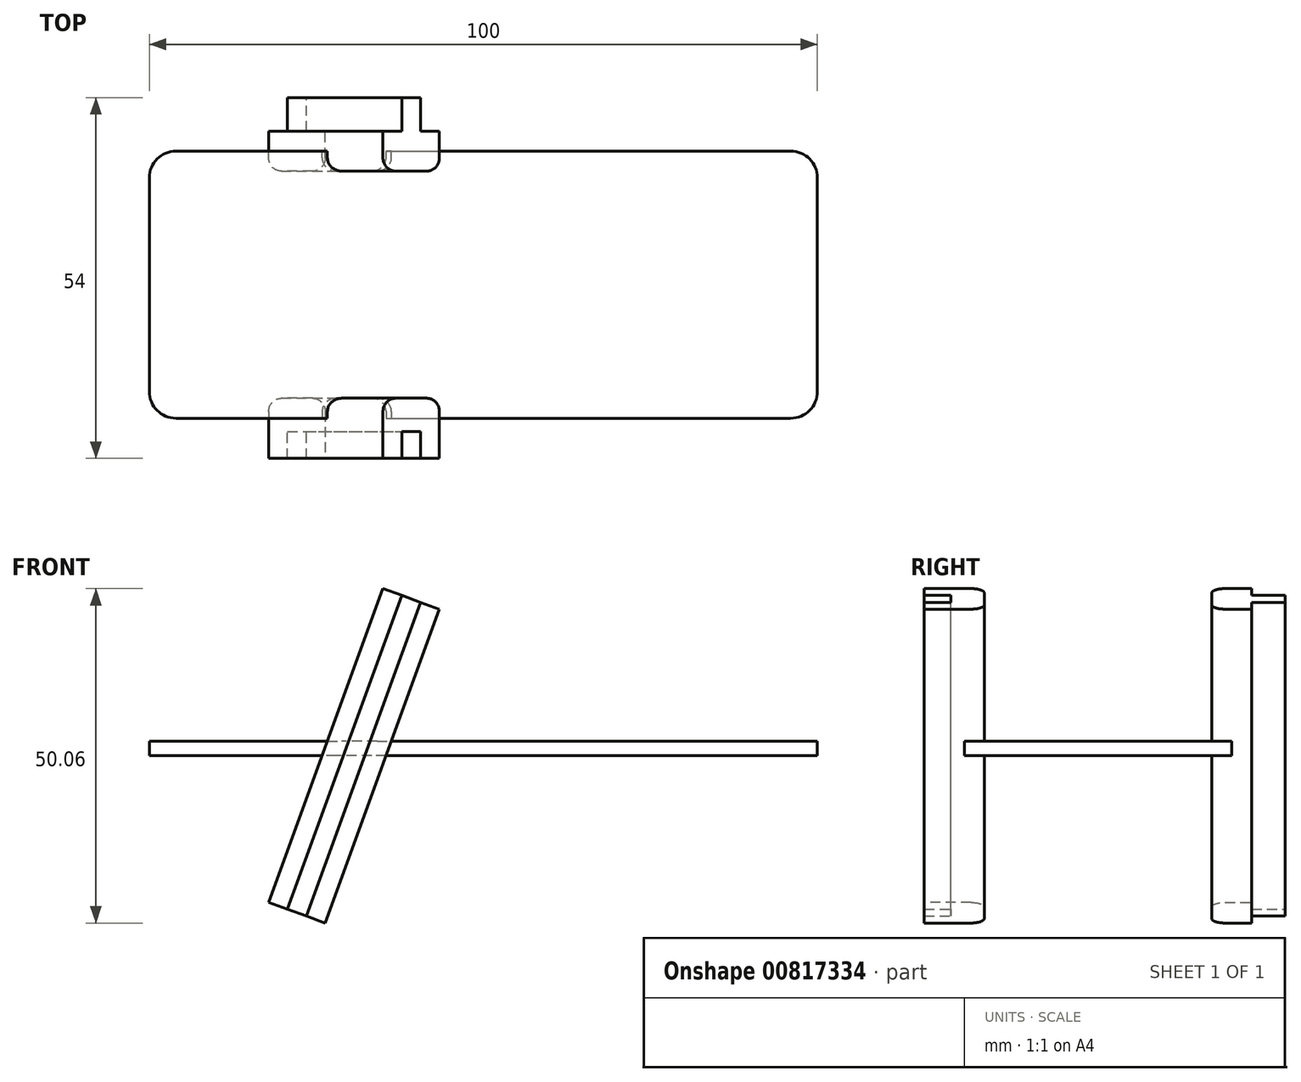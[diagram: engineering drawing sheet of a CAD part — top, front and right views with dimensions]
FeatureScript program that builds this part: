
annotation { "Feature Type Name" : "Feature", "Feature Type Description" : "" }
export const myFeature = defineFeature(function(context is Context, id is Id, definition is map)
    precondition{}
    {
        {
            var Q0;
            Q0=qCreatedBy(makeId("Top.planeOp"),FACE);
            var sketch = newSketch(context, id + "F0", { "sketchPlane" : qUnion([Q0])});
            skLineSegment(sketch, "E0.bottom", {"start": v(-43.22, 17.39) * mm, "end": v(-12.57, 17.39) * mm});
            skLineSegment(sketch, "E0.top", {"start": v(-43.22, -22.61) * mm, "end": v(-12.57, -22.61) * mm});
            skLineSegment(sketch, "E0.left", {"start": v(-43.22, 17.39) * mm, "end": v(-43.22, -22.61) * mm});
            skLineSegment(sketch, "E1", {"start": v(-12.57, 17.39) * mm, "end": v(-12.57, -22.61) * mm});
            skLineSegment(sketch, "E2", {"start": v(-12.57, 17.39) * mm, "end": v(56.78, 17.39) * mm});
            skLineSegment(sketch, "E3", {"start": v(56.78, 17.39) * mm, "end": v(56.78, -22.61) * mm});
            skLineSegment(sketch, "E4", {"start": v(56.78, -22.61) * mm, "end": v(-12.57, -22.61) * mm});
            skSolve(sketch);
        }
        {
            var Q0;
            {var subQ0=sQuery(id+"F0.wireOp",EDGE,"E0.left");Q0=makeQuery(id+"F0.imprint","IMPRINT",FACE,{"disambiguationData":[TD([[makeQuery(id+"F0.imprint","IMPRINT",EDGE,{"derivedFrom":subQ0}),1.0]])]});}
            var Q1;
            {var subQ0=sQuery(id+"F0.wireOp",EDGE,"E0.right");Q1=makeQuery(id+"F0.imprint","IMPRINT",FACE,{"disambiguationData":[TD([[makeQuery(id+"F0.imprint","IMPRINT",EDGE,{"derivedFrom":subQ0}),-1.0]])]});}
            var Q2;
            Q2=makeQuery(id+"F0.imprint","IMPRINT",FACE,{"disambiguationData":[TD([[makeQuery(id+"F0.imprint","IMPRINT",EDGE,{"derivedFrom":sQuery(id+"F0.wireOp",EDGE,"E1")}),1.0]])]});
            extrude(context, id + "F1", {"entities" : qUnion([Q0, Q1, Q2]), "depth" : 2.2 * mm, "offsetDistance" : 25 * mm});
        }
        {
            var Q0;
            Q0=qCreatedBy(makeId("Top.planeOp"),FACE);
            var Q1;
            Q1=sQuery(id+"F0.wireOp",EDGE,"E1");
            cPlane(context, id + "F2", {"entities" : qUnion([Q0, Q1]), "cplaneType" : CPlaneType.LINE_ANGLE, "offset" : 0 * mm, "angle" : 20 * degree, "oppositeDirection" : true, "width" : 150 * mm, "height" : 150 * mm});
        }
        {
            var Q0;
            Q0=qCreatedBy(id+"F2.planeOp",FACE);
            var sketch = newSketch(context, id + "F3", { "sketchPlane" : qUnion([Q0])});
            skLineSegment(sketch, "E5", {"start": v(-7.32, -14.39) * mm, "end": v(-11.82, -14.39) * mm});
            skLineSegment(sketch, "E6", {"start": v(-7.32, -14.39) * mm, "end": v(-7.32, -20.39) * mm});
            skLineSegment(sketch, "E7", {"start": v(-10.32, -20.39) * mm, "end": v(-7.32, -20.39) * mm});
            skLineSegment(sketch, "E8", {"start": v(-10.32, -20.39) * mm, "end": v(-10.32, -25.39) * mm});
            skLineSegment(sketch, "E9", {"start": v(-11.82, -25.39) * mm, "end": v(-10.32, -25.39) * mm});
            skLineSegment(sketch, "E10", {"start": v(-11.82, -25.39) * mm, "end": v(-11.82, -14.39) * mm});
            skLineSegment(sketch, "E11.MirrorCS", {"start": v(-11.82, -25.39) * mm, "end": v(-13.32, -25.39) * mm});
            skLineSegment(sketch, "E12.MirrorCS", {"start": v(-13.32, -20.39) * mm, "end": v(-13.32, -25.39) * mm});
            skLineSegment(sketch, "E13.MirrorCS", {"start": v(-13.32, -20.39) * mm, "end": v(-16.32, -20.39) * mm});
            skLineSegment(sketch, "E14.MirrorCS", {"start": v(-16.32, -14.39) * mm, "end": v(-16.32, -20.39) * mm});
            skLineSegment(sketch, "E15.MirrorCS", {"start": v(-16.32, -14.39) * mm, "end": v(-11.82, -14.39) * mm});
            skLineSegment(sketch, "E16", {"start": v(-7.32, 19.61) * mm, "end": v(-11.82, 19.61) * mm});
            skLineSegment(sketch, "E17", {"start": v(-7.32, 19.61) * mm, "end": v(-7.32, 28.61) * mm});
            skLineSegment(sketch, "E18", {"start": v(-10.32, 28.61) * mm, "end": v(-7.32, 28.61) * mm});
            skLineSegment(sketch, "E19", {"start": v(-10.32, 28.61) * mm, "end": v(-10.32, 24.61) * mm});
            skLineSegment(sketch, "E20", {"start": v(-11.82, 24.61) * mm, "end": v(-10.32, 24.61) * mm});
            skLineSegment(sketch, "E21", {"start": v(-11.82, 24.61) * mm, "end": v(-11.82, 19.61) * mm});
            skLineSegment(sketch, "E22.MirrorCS", {"start": v(-16.32, 19.61) * mm, "end": v(-11.82, 19.61) * mm});
            skLineSegment(sketch, "E23.MirrorCS", {"start": v(-16.32, 19.61) * mm, "end": v(-16.32, 28.61) * mm});
            skLineSegment(sketch, "E24.MirrorCS", {"start": v(-13.32, 28.61) * mm, "end": v(-16.32, 28.61) * mm});
            skLineSegment(sketch, "E25.MirrorCS", {"start": v(-13.32, 28.61) * mm, "end": v(-13.32, 24.61) * mm});
            skLineSegment(sketch, "E26.MirrorCS", {"start": v(-11.82, 24.61) * mm, "end": v(-13.32, 24.61) * mm});
            skSolve(sketch);
        }
        {
            var Q0;
            Q0=makeQuery(id+"F3.imprint","IMPRINT",FACE,{"disambiguationData":[TD([[makeQuery(id+"F3.imprint","IMPRINT",EDGE,{"derivedFrom":sQuery(id+"F3.wireOp",EDGE,"E5")}),1.0]])]});
            var Q1;
            Q1=makeQuery(id+"F3.imprint","IMPRINT",FACE,{"disambiguationData":[TD([[makeQuery(id+"F3.imprint","IMPRINT",EDGE,{"derivedFrom":sQuery(id+"F3.wireOp",EDGE,"E10")}),-1.0]])]});
            var Q2;
            Q2=makeQuery(id+"F3.imprint","IMPRINT",FACE,{"disambiguationData":[TD([[makeQuery(id+"F3.imprint","IMPRINT",EDGE,{"derivedFrom":sQuery(id+"F3.wireOp",EDGE,"E16")}),-1.0]])]});
            var Q3;
            Q3=makeQuery(id+"F3.imprint","IMPRINT",FACE,{"disambiguationData":[TD([[makeQuery(id+"F3.imprint","IMPRINT",EDGE,{"derivedFrom":sQuery(id+"F3.wireOp",EDGE,"E21")}),1.0]])]});
            var Q4;
            Q4=makeQuery(id+"F3.imprint","IMPRINT",FACE,{"disambiguationData":[TD([[makeQuery(id+"F3.imprint","IMPRINT",EDGE,{"derivedFrom":sQuery(id+"F3.wireOp",EDGE,"E10")}),1.0]])]});
            var Q5;
            Q5=makeQuery(id+"F3.imprint","IMPRINT",FACE,{"disambiguationData":[TD([[makeQuery(id+"F3.imprint","IMPRINT",EDGE,{"derivedFrom":sQuery(id+"F3.wireOp",EDGE,"E21")}),-1.0]])]});
            extrude(context, id + "F4", {"entities" : qUnion([Q0, Q1, Q2, Q3, Q4, Q5]), "operationType" : NewBodyOperationType.ADD, "depth" : 25 * mm, "offsetDistance" : 25 * mm, "hasSecondDirection" : true, "secondDirectionOppositeDirection" : true, "secondDirectionDepth" : 25 * mm});
        }
        {
            var Q0;
            Q0=makeQuery(id+"F1.opExtrude","SWEPT_EDGE",EDGE,{"disambiguationData":[OSD([sQuery(id+"F0.wireOp",EDGE,"E0.bottom"),sQuery(id+"F0.wireOp",EDGE,"E0.left")])]});
            var Q1;
            Q1=makeQuery(id+"F1.opExtrude","SWEPT_EDGE",EDGE,{"disambiguationData":[OSD([sQuery(id+"F0.wireOp",EDGE,"E0.top"),sQuery(id+"F0.wireOp",EDGE,"E0.left")])]});
            var Q2;
            Q2=makeQuery(id+"F1.opExtrude","SWEPT_EDGE",EDGE,{"disambiguationData":[OSD([sQuery(id+"F0.wireOp",EDGE,"E3"),sQuery(id+"F0.wireOp",EDGE,"E4")])]});
            var Q3;
            Q3=makeQuery(id+"F1.opExtrude","SWEPT_EDGE",EDGE,{"disambiguationData":[OSD([sQuery(id+"F0.wireOp",EDGE,"E2"),sQuery(id+"F0.wireOp",EDGE,"E3")])]});
            fillet(context, id + "F5", {"entities" : qUnion([Q0, Q1, Q2, Q3]), "radius" : 4 * mm, "tangentPropagation" : true, "allowEdgeOverflow" : false});
        }
        {
            var Q0;
            {var subQ1=sQuery(id+"F3.wireOp",EDGE,"E16");var subQ2=sQuery(id+"F3.wireOp",EDGE,"E17");Q0=makeQuery(id+"F4.boolean.opBoolean","SPLIT",EDGE,{"disambiguationData":[TD([makeQuery(id+"F1.opExtrude","CAP_FACE",FACE,{"disambiguationData":[OSD([sQuery(id+"F0.wireOp",EDGE,"E0.bottom"),sQuery(id+"F0.wireOp",EDGE,"E0.top"),sQuery(id+"F0.wireOp",EDGE,"E0.left"),sQuery(id+"F0.wireOp",EDGE,"E2"),sQuery(id+"F0.wireOp",EDGE,"E3"),sQuery(id+"F0.wireOp",EDGE,"E4")])],"isStart":false})])],"derivedFrom":makeQuery(id+"F4.opExtrude","SWEPT_EDGE",EDGE,{"disambiguationData":[OSD([subQ1,subQ2])]})});}
            var Q1;
            {var subQ0=sQuery(id+"F3.wireOp",EDGE,"E22.MirrorCS");var subQ2=sQuery(id+"F3.wireOp",EDGE,"E23.MirrorCS");Q1=makeQuery(id+"F4.boolean.opBoolean","SPLIT",EDGE,{"disambiguationData":[TD([makeQuery(id+"F1.opExtrude","CAP_FACE",FACE,{"disambiguationData":[OSD([sQuery(id+"F0.wireOp",EDGE,"E0.bottom"),sQuery(id+"F0.wireOp",EDGE,"E0.top"),sQuery(id+"F0.wireOp",EDGE,"E0.left"),sQuery(id+"F0.wireOp",EDGE,"E2"),sQuery(id+"F0.wireOp",EDGE,"E3"),sQuery(id+"F0.wireOp",EDGE,"E4")])],"isStart":false})])],"derivedFrom":makeQuery(id+"F4.opExtrude","SWEPT_EDGE",EDGE,{"disambiguationData":[OSD([subQ0,subQ2])]})});}
            var Q2;
            {var subQ1=sQuery(id+"F3.wireOp",EDGE,"E5");var subQ2=sQuery(id+"F3.wireOp",EDGE,"E6");Q2=makeQuery(id+"F4.boolean.opBoolean","SPLIT",EDGE,{"disambiguationData":[TD([makeQuery(id+"F1.opExtrude","CAP_FACE",FACE,{"disambiguationData":[OSD([sQuery(id+"F0.wireOp",EDGE,"E0.bottom"),sQuery(id+"F0.wireOp",EDGE,"E0.top"),sQuery(id+"F0.wireOp",EDGE,"E0.left"),sQuery(id+"F0.wireOp",EDGE,"E2"),sQuery(id+"F0.wireOp",EDGE,"E3"),sQuery(id+"F0.wireOp",EDGE,"E4")])],"isStart":false})])],"derivedFrom":makeQuery(id+"F4.opExtrude","SWEPT_EDGE",EDGE,{"disambiguationData":[OSD([subQ1,subQ2])]})});}
            var Q3;
            {var subQ1=sQuery(id+"F3.wireOp",EDGE,"E6");var subQ2=sQuery(id+"F3.wireOp",EDGE,"E5");Q3=makeQuery(id+"F4.boolean.opBoolean","SPLIT",EDGE,{"disambiguationData":[TD([makeQuery(id+"F1.opExtrude","CAP_FACE",FACE,{"disambiguationData":[OSD([sQuery(id+"F0.wireOp",EDGE,"E0.bottom"),sQuery(id+"F0.wireOp",EDGE,"E0.top"),sQuery(id+"F0.wireOp",EDGE,"E0.left"),sQuery(id+"F0.wireOp",EDGE,"E2"),sQuery(id+"F0.wireOp",EDGE,"E3"),sQuery(id+"F0.wireOp",EDGE,"E4")])],"isStart":true})])],"derivedFrom":makeQuery(id+"F4.opExtrude","SWEPT_EDGE",EDGE,{"disambiguationData":[OSD([subQ2,subQ1])]})});}
            var Q4;
            {var subQ0=sQuery(id+"F3.wireOp",EDGE,"E15.MirrorCS");var subQ2=sQuery(id+"F3.wireOp",EDGE,"E14.MirrorCS");Q4=makeQuery(id+"F4.boolean.opBoolean","SPLIT",EDGE,{"disambiguationData":[TD([makeQuery(id+"F1.opExtrude","CAP_FACE",FACE,{"disambiguationData":[OSD([sQuery(id+"F0.wireOp",EDGE,"E0.bottom"),sQuery(id+"F0.wireOp",EDGE,"E0.top"),sQuery(id+"F0.wireOp",EDGE,"E0.left"),sQuery(id+"F0.wireOp",EDGE,"E2"),sQuery(id+"F0.wireOp",EDGE,"E3"),sQuery(id+"F0.wireOp",EDGE,"E4")])],"isStart":false})])],"derivedFrom":makeQuery(id+"F4.opExtrude","SWEPT_EDGE",EDGE,{"disambiguationData":[OSD([subQ2,subQ0])]})});}
            var Q5;
            {var subQ0=sQuery(id+"F3.wireOp",EDGE,"E15.MirrorCS");var subQ1=sQuery(id+"F3.wireOp",EDGE,"E14.MirrorCS");Q5=makeQuery(id+"F4.boolean.opBoolean","SPLIT",EDGE,{"disambiguationData":[TD([makeQuery(id+"F1.opExtrude","CAP_FACE",FACE,{"disambiguationData":[OSD([sQuery(id+"F0.wireOp",EDGE,"E0.bottom"),sQuery(id+"F0.wireOp",EDGE,"E0.top"),sQuery(id+"F0.wireOp",EDGE,"E0.left"),sQuery(id+"F0.wireOp",EDGE,"E2"),sQuery(id+"F0.wireOp",EDGE,"E3"),sQuery(id+"F0.wireOp",EDGE,"E4")])],"isStart":true})])],"derivedFrom":makeQuery(id+"F4.opExtrude","SWEPT_EDGE",EDGE,{"disambiguationData":[OSD([subQ1,subQ0])]})});}
            var Q6;
            {var subQ0=sQuery(id+"F3.wireOp",EDGE,"E23.MirrorCS");var subQ1=sQuery(id+"F3.wireOp",EDGE,"E22.MirrorCS");Q6=makeQuery(id+"F4.boolean.opBoolean","SPLIT",EDGE,{"disambiguationData":[TD([makeQuery(id+"F1.opExtrude","CAP_FACE",FACE,{"disambiguationData":[OSD([sQuery(id+"F0.wireOp",EDGE,"E0.bottom"),sQuery(id+"F0.wireOp",EDGE,"E0.top"),sQuery(id+"F0.wireOp",EDGE,"E0.left"),sQuery(id+"F0.wireOp",EDGE,"E2"),sQuery(id+"F0.wireOp",EDGE,"E3"),sQuery(id+"F0.wireOp",EDGE,"E4")])],"isStart":true})])],"derivedFrom":makeQuery(id+"F4.opExtrude","SWEPT_EDGE",EDGE,{"disambiguationData":[OSD([subQ1,subQ0])]})});}
            var Q7;
            {var subQ1=sQuery(id+"F3.wireOp",EDGE,"E17");var subQ2=sQuery(id+"F3.wireOp",EDGE,"E16");Q7=makeQuery(id+"F4.boolean.opBoolean","SPLIT",EDGE,{"disambiguationData":[TD([makeQuery(id+"F1.opExtrude","CAP_FACE",FACE,{"disambiguationData":[OSD([sQuery(id+"F0.wireOp",EDGE,"E0.bottom"),sQuery(id+"F0.wireOp",EDGE,"E0.top"),sQuery(id+"F0.wireOp",EDGE,"E0.left"),sQuery(id+"F0.wireOp",EDGE,"E2"),sQuery(id+"F0.wireOp",EDGE,"E3"),sQuery(id+"F0.wireOp",EDGE,"E4")])],"isStart":true})])],"derivedFrom":makeQuery(id+"F4.opExtrude","SWEPT_EDGE",EDGE,{"disambiguationData":[OSD([subQ2,subQ1])]})});}
            fillet(context, id + "F6", {"entities" : qUnion([Q0, Q1, Q2, Q3, Q4, Q5, Q6, Q7]), "radius" : 2 * mm, "tangentPropagation" : true, "allowEdgeOverflow" : false});
        }
    });
